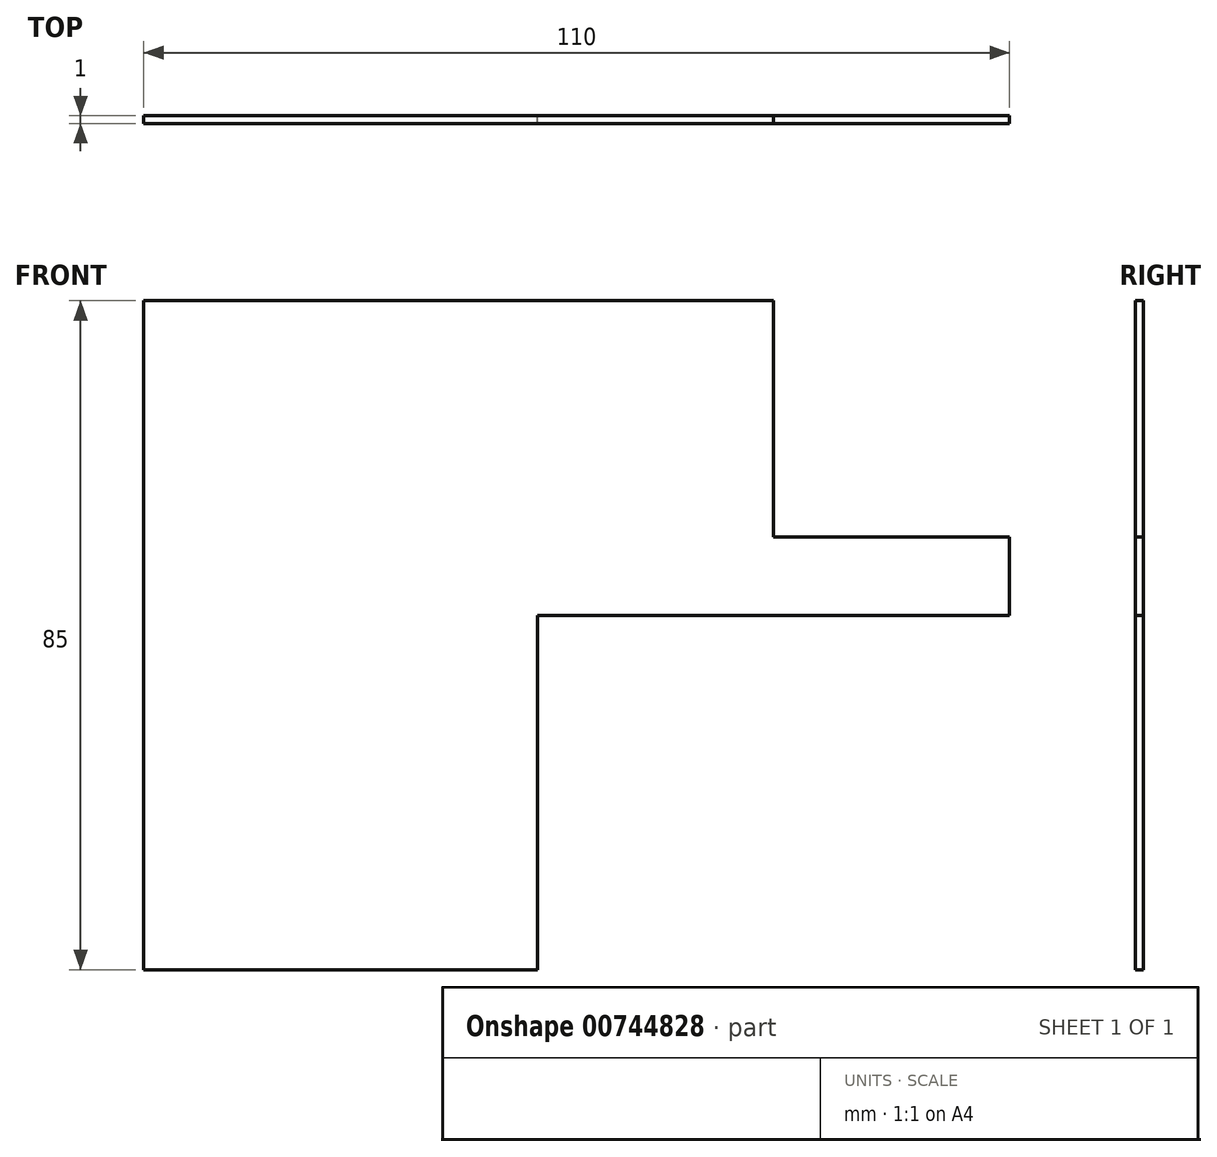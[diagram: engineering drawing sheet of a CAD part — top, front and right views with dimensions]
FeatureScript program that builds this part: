
annotation { "Feature Type Name" : "Feature", "Feature Type Description" : "" }
export const myFeature = defineFeature(function(context is Context, id is Id, definition is map)
    precondition{}
    {
        {
            var Q0;
            Q0=qCreatedBy(makeId("Front.planeOp"),FACE);
            var sketch = newSketch(context, id + "F0", { "sketchPlane" : qUnion([Q0])});
            skLineSegment(sketch, "E0", {"start": v(0, 0) * mm, "end": v(-5, 0) * mm});
            skLineSegment(sketch, "E1", {"start": v(-5, 0) * mm, "end": v(-5, 30) * mm});
            skLineSegment(sketch, "E2", {"start": v(-5, 30) * mm, "end": v(-85, 30) * mm});
            skLineSegment(sketch, "E3", {"start": v(-85, 30) * mm, "end": v(-85, -55) * mm});
            skLineSegment(sketch, "E4", {"start": v(-85, -55) * mm, "end": v(-35, -55) * mm});
            skLineSegment(sketch, "E5", {"start": v(-35, -55) * mm, "end": v(-35, -10) * mm});
            skLineSegment(sketch, "E6", {"start": v(-35, -10) * mm, "end": v(0, -10) * mm});
            skLineSegment(sketch, "E7", {"start": v(0, -10) * mm, "end": v(25, -10) * mm});
            skLineSegment(sketch, "E8", {"start": v(25, -10) * mm, "end": v(25, 0) * mm});
            skLineSegment(sketch, "E9", {"start": v(25, 0) * mm, "end": v(0, 0) * mm});
            skSolve(sketch);
        }
        {
            var Q0;
            Q0=makeQuery(id+"F0.imprint","IMPRINT",FACE,{"disambiguationData":[TD([[makeQuery(id+"F0.imprint","IMPRINT",EDGE,{"derivedFrom":sQuery(id+"F0.wireOp",EDGE,"E0")}),1.0]])]});
            extrude(context, id + "F1", {"entities" : qUnion([Q0]), "endBound" : BoundingType.SYMMETRIC, "depth" : 1 * mm, "offsetDistance" : 25 * mm});
        }
    });
